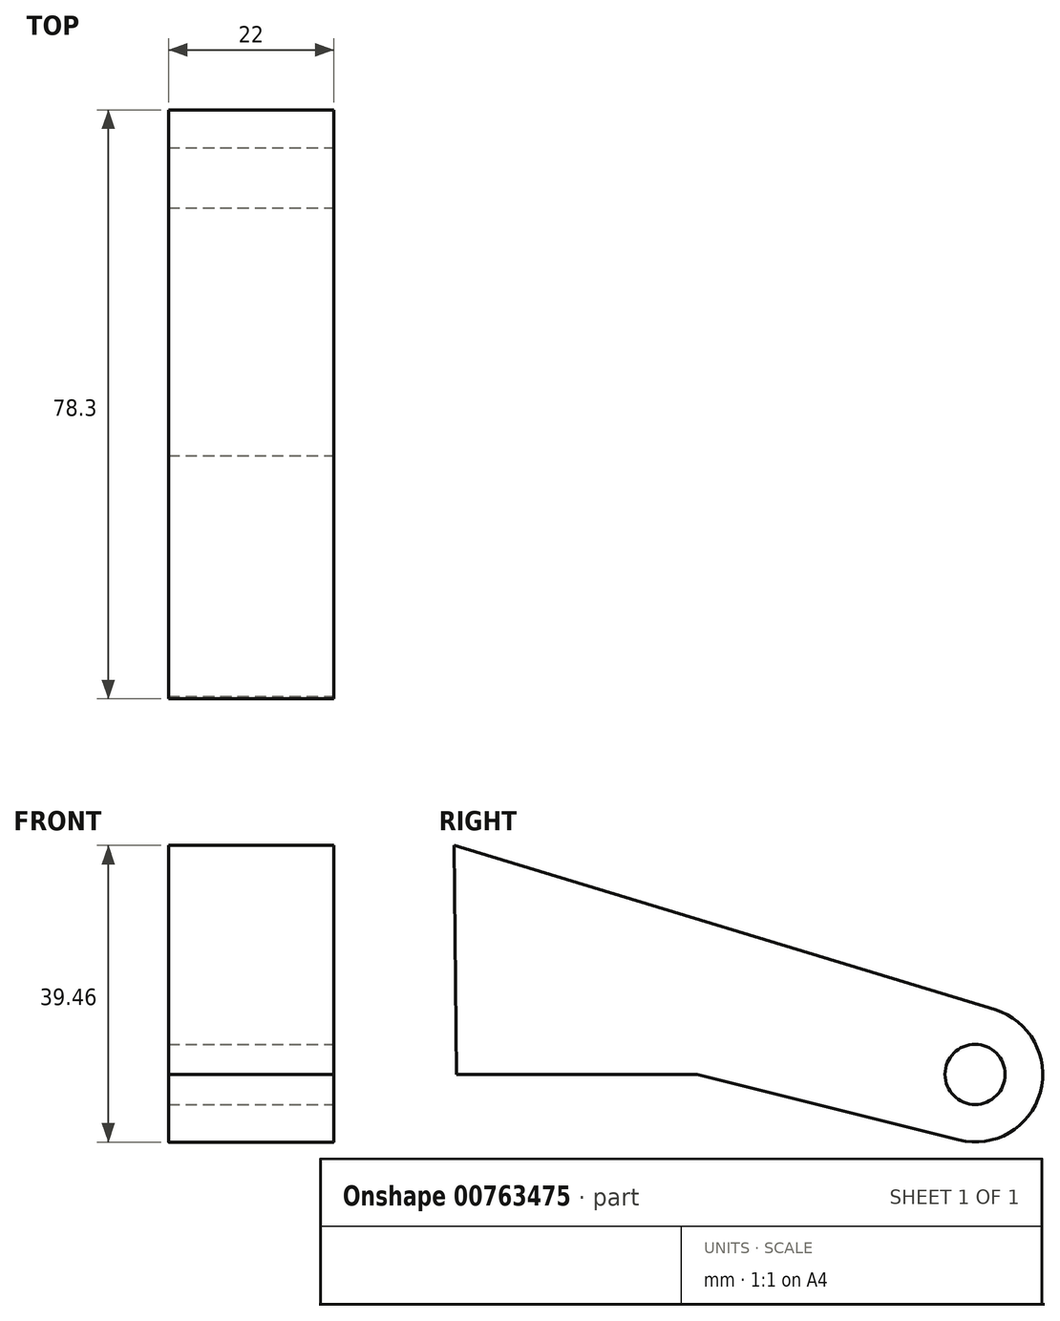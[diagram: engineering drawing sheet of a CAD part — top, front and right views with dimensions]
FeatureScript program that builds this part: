
annotation { "Feature Type Name" : "Feature", "Feature Type Description" : "" }
export const myFeature = defineFeature(function(context is Context, id is Id, definition is map)
    precondition{}
    {
        {
            var Q0;
            Q0=qCreatedBy(makeId("Right.planeOp"),FACE);
            var sketch = newSketch(context, id + "F0", { "sketchPlane" : qUnion([Q0])});
            skLineSegment(sketch, "E0", {"start": v(-56.3, 18.28) * mm, "end": v(-24.3, 18.28) * mm});
            skLineSegment(sketch, "E1", {"start": v(15.31, 26.9) * mm, "end": v(-56.61, 48.74) * mm});
            skLineSegment(sketch, "E2", {"start": v(-56.61, 48.74) * mm, "end": v(-56.3, 18.28) * mm});
            skLineSegment(sketch, "E3", {"start": v(-24.3, 18.28) * mm, "end": v(10.5, 9.55) * mm});
            skLineSegment(sketch, "E4", {"start": v(-56.3, 18.28) * mm, "end": v(12.7, 18.28) * mm, "construction": true});
            skCircle(sketch, "E5", {"center": v(12.7, 18.28) * mm, "radius": 4 * mm});
            skArc(sketch, "E6", {"start": v(10.5, 9.55) * mm, "mid": v(21.37, 15.88) * mm, "end": v(15.31, 26.9) * mm});
            skSolve(sketch);
        }
        {
            var Q0;
            Q0=makeQuery(id+"F0.imprint","IMPRINT",FACE,{"disambiguationData":[TD([[makeQuery(id+"F0.imprint","IMPRINT",EDGE,{"derivedFrom":sQuery(id+"F0.wireOp",EDGE,"E0")}),1.0]])]});
            extrude(context, id + "F1", {"entities" : qUnion([Q0]), "oppositeDirection" : true, "depth" : 22 * mm, "offsetDistance" : 25 * mm});
        }
    });
